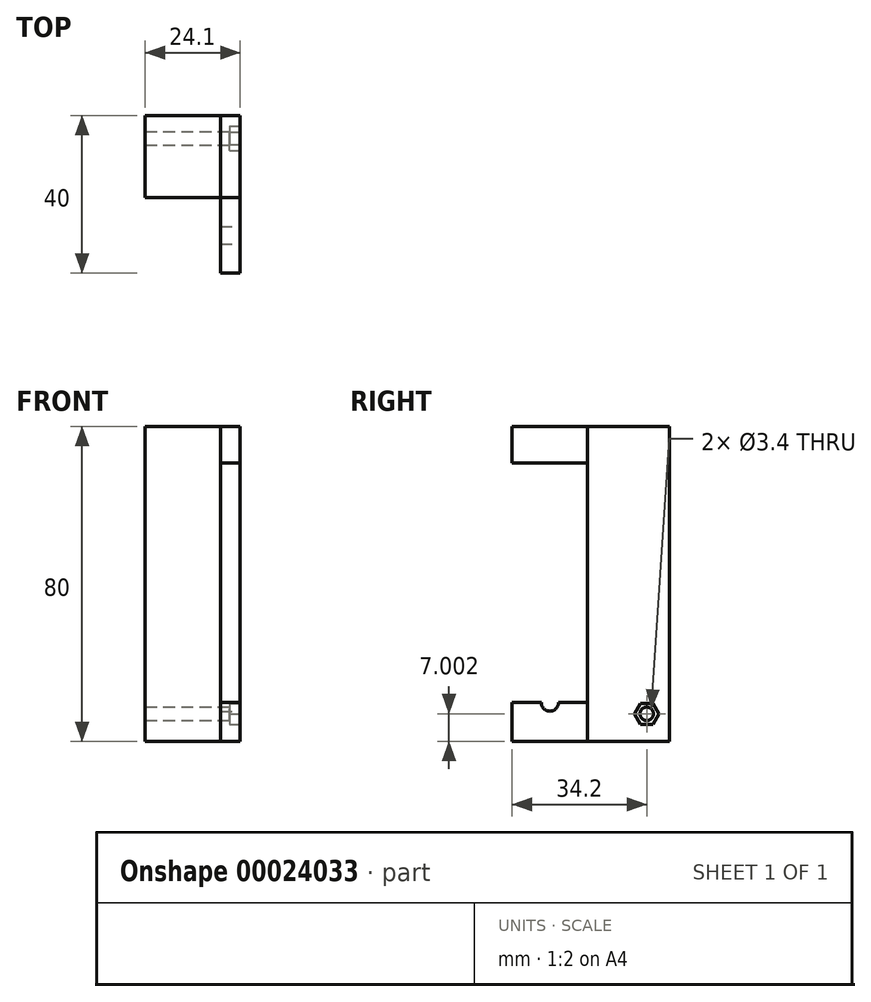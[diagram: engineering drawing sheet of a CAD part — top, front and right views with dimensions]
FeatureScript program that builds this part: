
annotation { "Feature Type Name" : "Feature", "Feature Type Description" : "" }
export const myFeature = defineFeature(function(context is Context, id is Id, definition is map)
    precondition{}
    {
        {
            var Q0;
            Q0=qCreatedBy(makeId("Right.planeOp"),FACE);
            var sketch = newSketch(context, id + "F0", { "sketchPlane" : qUnion([Q0])});
            skLineSegment(sketch, "E0", {"start": v(-57.68, 41.75) * mm, "end": v(-17.68, 41.75) * mm});
            skLineSegment(sketch, "E1", {"start": v(-17.68, 41.75) * mm, "end": v(-17.68, -38.25) * mm});
            skLineSegment(sketch, "E2", {"start": v(-17.68, -38.25) * mm, "end": v(-57.68, -38.25) * mm});
            skLineSegment(sketch, "E3", {"start": v(-57.68, -38.25) * mm, "end": v(-57.68, 41.75) * mm});
            skLineSegment(sketch, "E4", {"start": v(-38.48, 41.75) * mm, "end": v(-38.48, -38.25) * mm});
            skLineSegment(sketch, "E5", {"start": v(-38.48, -38.25) * mm, "end": v(-17.68, -38.25) * mm});
            skLineSegment(sketch, "E6", {"start": v(-17.68, 41.75) * mm, "end": v(-38.48, 41.75) * mm});
            skLineSegment(sketch, "E7", {"start": v(-57.68, 41.75) * mm, "end": v(-38.48, 41.75) * mm});
            skLineSegment(sketch, "E8", {"start": v(-38.48, -38.25) * mm, "end": v(-57.68, -38.25) * mm});
            skSolve(sketch);
        }
        {
            var Q0;
            Q0=makeQuery(id+"F0.imprint","IMPRINT",FACE,{"disambiguationData":[TD([[makeQuery(id+"F0.imprint","IMPRINT",EDGE,{"derivedFrom":sQuery(id+"F0.wireOp",EDGE,"E3")}),-1.0]])]});
            extrude(context, id + "F1", {"entities" : qUnion([Q0]), "depth" : 5 * mm});
        }
        {
            var Q0;
            Q0=makeQuery(id+"F0.imprint","IMPRINT",FACE,{"disambiguationData":[TD([[makeQuery(id+"F0.imprint","IMPRINT",EDGE,{"derivedFrom":sQuery(id+"F0.wireOp",EDGE,"E1")}),-1.0]])]});
            extrude(context, id + "F2", {"entities" : qUnion([Q0]), "operationType" : NewBodyOperationType.ADD, "oppositeDirection" : true, "depth" : 19.1 * mm});
        }
        {
            var Q0;
            Q0=makeQuery(id+"F0.imprint","IMPRINT",FACE,{"disambiguationData":[TD([[makeQuery(id+"F0.imprint","IMPRINT",EDGE,{"derivedFrom":sQuery(id+"F0.wireOp",EDGE,"E1")}),-1.0]])]});
            extrude(context, id + "F3", {"entities" : qUnion([Q0]), "depth" : 5 * mm});
        }
        {
            var Q0;
            Q0=makeQuery(id+"F1.opExtrude","CAP_FACE",FACE,{"disambiguationData":[OSD([sQuery(id+"F0.wireOp",EDGE,"E3"),sQuery(id+"F0.wireOp",EDGE,"E4"),sQuery(id+"F0.wireOp",EDGE,"E8"),sQuery(id+"F0.wireOp",EDGE,"E7")])],"isStart":false});
            var sketch = newSketch(context, id + "F4", { "sketchPlane" : qUnion([Q0])});
            skLineSegment(sketch, "E9", {"start": v(-48.08, 41.75) * mm, "end": v(-48.08, -38.25) * mm});
            skLineSegment(sketch, "E10", {"start": v(-57.68, 32.42) * mm, "end": v(-38.48, 32.42) * mm});
            skLineSegment(sketch, "E11", {"start": v(-57.68, -28.38) * mm, "end": v(-38.48, -28.38) * mm});
            skCircle(sketch, "E12", {"center": v(-48.08, 32.42) * mm, "radius": 2.2 * mm});
            skCircle(sketch, "E13", {"center": v(-48.08, -28.38) * mm, "radius": 2.2 * mm});
            skSolve(sketch);
        }
        {
            var Q0;
            {var subQ1=sQuery(id+"F4.wireOp",EDGE,"E10");var subQ3=sQuery(id+"F4.wireOp",EDGE,"E9");var subQ5=makeQuery(id+"F4.imprint","INTERSECT",VERTEX,{"derivedFrom":[subQ3,subQ1]});Q0=makeQuery(id+"F4.imprint","IMPRINT",FACE,{"disambiguationData":[TD([[makeQuery(id+"F4.imprint","IMPRINT",EDGE,{"disambiguationData":[TD([[subQ5,-1.0]])],"derivedFrom":subQ3}),1.0]])]});}
            var Q1;
            {var subQ0=sQuery(id+"F4.wireOp",EDGE,"E12");var subQ3=sQuery(id+"F4.wireOp",EDGE,"E9");var subQ4=makeQuery(id+"F4.imprint","INTERSECT",VERTEX,{"disambiguationData":[OD(0.0)],"derivedFrom":[subQ3,subQ0]});Q1=makeQuery(id+"F4.imprint","IMPRINT",FACE,{"disambiguationData":[TD([[makeQuery(id+"F4.imprint","IMPRINT",EDGE,{"disambiguationData":[TD([[subQ4,-1.0]])],"derivedFrom":subQ3}),1.0]])]});}
            var Q2;
            {var subQ0=sQuery(id+"F4.wireOp",EDGE,"E12");var subQ3=sQuery(id+"F4.wireOp",EDGE,"E9");var subQ4=makeQuery(id+"F4.imprint","INTERSECT",VERTEX,{"disambiguationData":[OD(0.0)],"derivedFrom":[subQ3,subQ0]});Q2=makeQuery(id+"F4.imprint","IMPRINT",FACE,{"disambiguationData":[TD([[makeQuery(id+"F4.imprint","IMPRINT",EDGE,{"disambiguationData":[TD([[subQ4,-1.0]])],"derivedFrom":subQ3}),-1.0]])]});}
            var Q3;
            {var subQ1=sQuery(id+"F4.wireOp",EDGE,"E10");var subQ3=sQuery(id+"F4.wireOp",EDGE,"E9");var subQ5=makeQuery(id+"F4.imprint","INTERSECT",VERTEX,{"derivedFrom":[subQ3,subQ1]});Q3=makeQuery(id+"F4.imprint","IMPRINT",FACE,{"disambiguationData":[TD([[makeQuery(id+"F4.imprint","IMPRINT",EDGE,{"disambiguationData":[TD([[subQ5,-1.0]])],"derivedFrom":subQ3}),-1.0]])]});}
            var Q4;
            {var subQ1=sQuery(id+"F4.wireOp",EDGE,"E11");var subQ3=sQuery(id+"F4.wireOp",EDGE,"E9");var subQ5=makeQuery(id+"F4.imprint","INTERSECT",VERTEX,{"derivedFrom":[subQ3,subQ1]});Q4=makeQuery(id+"F4.imprint","IMPRINT",FACE,{"disambiguationData":[TD([[makeQuery(id+"F4.imprint","IMPRINT",EDGE,{"disambiguationData":[TD([[subQ5,-1.0]])],"derivedFrom":subQ3}),1.0]])]});}
            var Q5;
            {var subQ1=sQuery(id+"F4.wireOp",EDGE,"E11");var subQ3=sQuery(id+"F4.wireOp",EDGE,"E9");var subQ5=makeQuery(id+"F4.imprint","INTERSECT",VERTEX,{"derivedFrom":[subQ3,subQ1]});Q5=makeQuery(id+"F4.imprint","IMPRINT",FACE,{"disambiguationData":[TD([[makeQuery(id+"F4.imprint","IMPRINT",EDGE,{"disambiguationData":[TD([[subQ5,-1.0]])],"derivedFrom":subQ3}),-1.0]])]});}
            var Q6;
            {var subQ0=sQuery(id+"F4.wireOp",EDGE,"E13");var subQ3=sQuery(id+"F4.wireOp",EDGE,"E9");var subQ4=makeQuery(id+"F4.imprint","INTERSECT",VERTEX,{"disambiguationData":[OD(0.0)],"derivedFrom":[subQ3,subQ0]});Q6=makeQuery(id+"F4.imprint","IMPRINT",FACE,{"disambiguationData":[TD([[makeQuery(id+"F4.imprint","IMPRINT",EDGE,{"disambiguationData":[TD([[subQ4,-1.0]])],"derivedFrom":subQ3}),-1.0]])]});}
            var Q7;
            {var subQ0=sQuery(id+"F4.wireOp",EDGE,"E13");var subQ3=sQuery(id+"F4.wireOp",EDGE,"E9");var subQ4=makeQuery(id+"F4.imprint","INTERSECT",VERTEX,{"disambiguationData":[OD(0.0)],"derivedFrom":[subQ3,subQ0]});Q7=makeQuery(id+"F4.imprint","IMPRINT",FACE,{"disambiguationData":[TD([[makeQuery(id+"F4.imprint","IMPRINT",EDGE,{"disambiguationData":[TD([[subQ4,-1.0]])],"derivedFrom":subQ3}),1.0]])]});}
            extrude(context, id + "F5", {"entities" : qUnion([Q0, Q1, Q2, Q3, Q4, Q5, Q6, Q7]), "operationType" : NewBodyOperationType.REMOVE, "oppositeDirection" : true, "depth" : 7 * mm});
        }
        {
            var Q0;
            Q0=makeQuery(id+"F3.opExtrude","CAP_FACE",FACE,{"disambiguationData":[OSD([sQuery(id+"F0.wireOp",EDGE,"E1"),sQuery(id+"F0.wireOp",EDGE,"E4"),sQuery(id+"F0.wireOp",EDGE,"E5"),sQuery(id+"F0.wireOp",EDGE,"E6")])],"isStart":false});
            var sketch = newSketch(context, id + "F6", { "sketchPlane" : qUnion([Q0])});
            skLineSegment(sketch, "E14", {"start": v(-17.68, 41.75) * mm, "end": v(-17.68, -38.25) * mm});
            skLineSegment(sketch, "E15", {"start": v(-17.68, -38.25) * mm, "end": v(-23.48, -38.25) * mm});
            skLineSegment(sketch, "E16", {"start": v(-23.48, -38.25) * mm, "end": v(-23.48, 41.75) * mm});
            skLineSegment(sketch, "E17", {"start": v(-23.48, 41.75) * mm, "end": v(-17.68, 41.75) * mm});
            skLineSegment(sketch, "E18", {"start": v(-23.48, -31.25) * mm, "end": v(-17.68, -31.25) * mm});
            skLineSegment(sketch, "E19", {"start": v(-17.68, -31.25) * mm, "end": v(-17.68, -38.25) * mm});
            skCircle(sketch, "E20", {"center": v(-23.48, -31.25) * mm, "radius": 1.7 * mm});
            skSolve(sketch);
        }
        {
            var Q0;
            {var subQ1=sQuery(id+"F6.wireOp",EDGE,"E18");var subQ3=sQuery(id+"F6.wireOp",EDGE,"E16");var subQ5=makeQuery(id+"F6.imprint","INTERSECT",VERTEX,{"derivedFrom":[subQ3,subQ1]});Q0=makeQuery(id+"F6.imprint","IMPRINT",FACE,{"disambiguationData":[TD([[makeQuery(id+"F6.imprint","IMPRINT",EDGE,{"disambiguationData":[TD([[subQ5,1.0]])],"derivedFrom":subQ3}),-1.0]])]});}
            var Q1;
            {var subQ1=sQuery(id+"F6.wireOp",EDGE,"E16");var subQ4=makeQuery(id+"F6.imprint","INTERSECT",VERTEX,{"derivedFrom":[subQ1,sQuery(id+"F6.wireOp",EDGE,"E18")]});Q1=makeQuery(id+"F6.imprint","IMPRINT",FACE,{"disambiguationData":[TD([[makeQuery(id+"F6.imprint","IMPRINT",EDGE,{"disambiguationData":[TD([[subQ4,1.0]])],"derivedFrom":subQ1}),1.0]])]});}
            var Q2;
            {var subQ1=sQuery(id+"F6.wireOp",EDGE,"E18");var subQ3=sQuery(id+"F6.wireOp",EDGE,"E16");var subQ5=makeQuery(id+"F6.imprint","INTERSECT",VERTEX,{"derivedFrom":[subQ3,subQ1]});Q2=makeQuery(id+"F6.imprint","IMPRINT",FACE,{"disambiguationData":[TD([[makeQuery(id+"F6.imprint","IMPRINT",EDGE,{"disambiguationData":[TD([[subQ5,-1.0]])],"derivedFrom":subQ3}),-1.0]])]});}
            extrude(context, id + "F7", {"entities" : qUnion([Q0, Q1, Q2]), "operationType" : NewBodyOperationType.REMOVE, "oppositeDirection" : true, "depth" : 35 * mm});
        }
        {
            var Q0;
            Q0=makeQuery(id+"F3.opExtrude","CAP_FACE",FACE,{"disambiguationData":[OSD([sQuery(id+"F0.wireOp",EDGE,"E1"),sQuery(id+"F0.wireOp",EDGE,"E4"),sQuery(id+"F0.wireOp",EDGE,"E5"),sQuery(id+"F0.wireOp",EDGE,"E6")])],"isStart":false});
            var sketch = newSketch(context, id + "F8", { "sketchPlane" : qUnion([Q0])});
            skCircle(sketch, "E21.cCircle", {"center": v(-23.48, -31.25) * mm, "radius": 2.7 * mm, "construction": true});
            skLineSegment(sketch, "E21.0", {"start": v(-21.92, -33.95) * mm, "end": v(-25.04, -33.95) * mm});
            skLineSegment(sketch, "E21.1", {"start": v(-25.04, -33.95) * mm, "end": v(-26.6, -31.25) * mm});
            skLineSegment(sketch, "E21.2", {"start": v(-26.6, -31.25) * mm, "end": v(-25.04, -28.55) * mm});
            skLineSegment(sketch, "E21.3", {"start": v(-25.04, -28.55) * mm, "end": v(-21.92, -28.55) * mm});
            skLineSegment(sketch, "E21.4", {"start": v(-21.92, -28.55) * mm, "end": v(-20.36, -31.25) * mm});
            skLineSegment(sketch, "E21.5", {"start": v(-20.36, -31.25) * mm, "end": v(-21.92, -33.95) * mm});
            skPoint(sketch, "E21.0.midPoint", {"position": v(-23.48, -33.95) * mm});
            skSolve(sketch);
        }
        {
            var Q0;
            Q0=makeQuery(id+"F8.imprint","IMPRINT",FACE,{"disambiguationData":[TD([[makeQuery(id+"F8.imprint","IMPRINT",EDGE,{"derivedFrom":sQuery(id+"F8.wireOp",EDGE,"E21.0")}),-1.0]])]});
            extrude(context, id + "F9", {"entities" : qUnion([Q0]), "operationType" : NewBodyOperationType.REMOVE, "oppositeDirection" : true, "depth" : 2.7 * mm});
        }
    });
